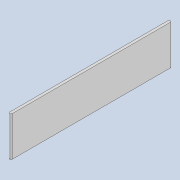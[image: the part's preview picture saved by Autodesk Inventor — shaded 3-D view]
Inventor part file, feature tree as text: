
AUTODESK INVENTOR PART (.ipt)
format: ipt  version: 2020 (Build 240168000, 168)  size: 75,776 bytes
history: native  units: mm
features: extrude x1, sketch x1
ambient origin geometry x8: Origin, YZ Plane, XZ Plane, XY Plane, X Axis, Y Axis, Z Axis, Center Point
bodies: Solid1 (feature_tree)
feature tree (2):
  extrude  "Extrusion1"  Depth=0.2mm
  sketch  "Sketch1"  dims[d0=12.0mm d1=0.2mm d2=3.0mm d3=0.0mm]
